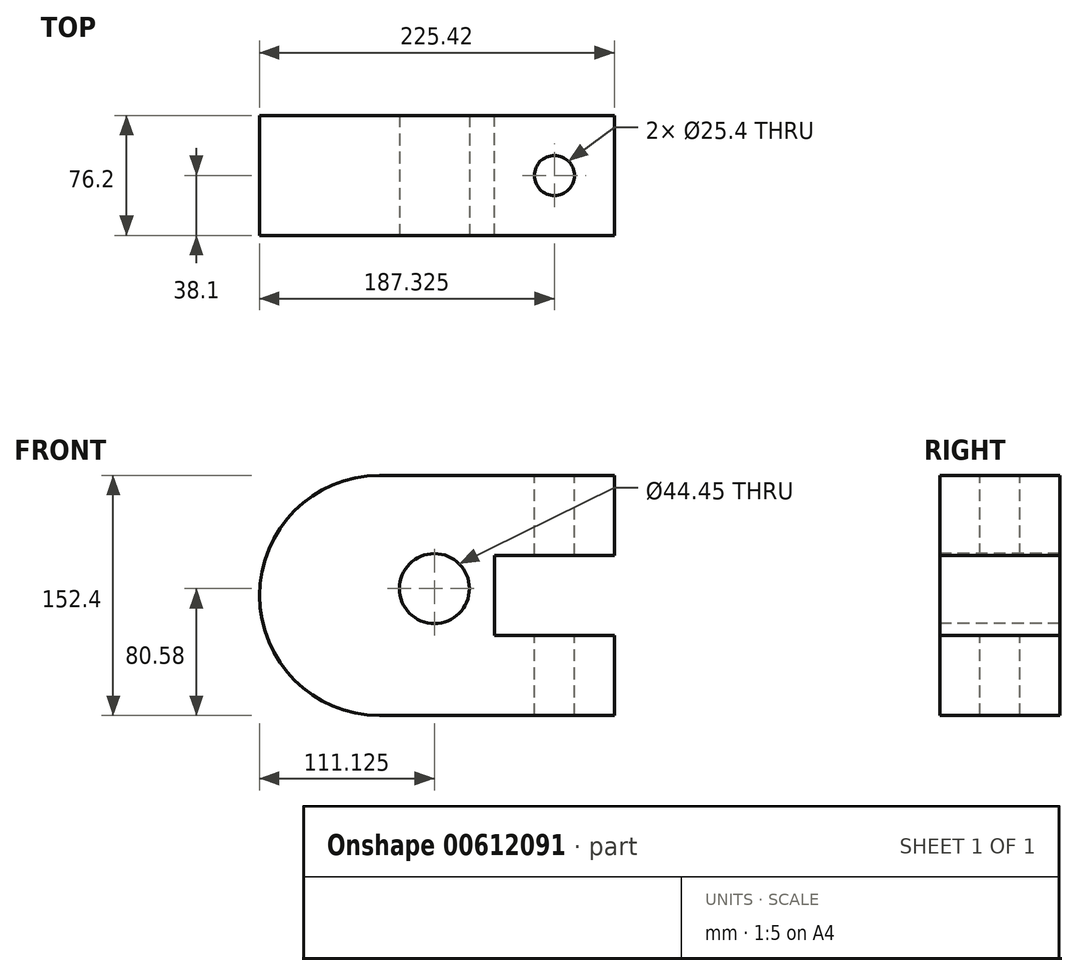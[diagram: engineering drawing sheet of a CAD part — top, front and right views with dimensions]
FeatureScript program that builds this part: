
annotation { "Feature Type Name" : "Feature", "Feature Type Description" : "" }
export const myFeature = defineFeature(function(context is Context, id is Id, definition is map)
    precondition{}
    {
        {
            var Q0;
            Q0=qCreatedBy(makeId("Front.planeOp"),FACE);
            var sketch = newSketch(context, id + "F0", { "sketchPlane" : qUnion([Q0])});
            skLineSegment(sketch, "E0", {"start": v(0, 0) * mm, "end": v(149.23, 0) * mm});
            skLineSegment(sketch, "E1", {"start": v(149.23, 0) * mm, "end": v(149.23, 50.8) * mm});
            skLineSegment(sketch, "E2", {"start": v(149.23, 50.8) * mm, "end": v(73.03, 50.8) * mm});
            skLineSegment(sketch, "E3", {"start": v(73.03, 50.8) * mm, "end": v(73.03, 101.6) * mm});
            skLineSegment(sketch, "E4", {"start": v(73.03, 101.6) * mm, "end": v(149.23, 101.6) * mm});
            skLineSegment(sketch, "E5", {"start": v(149.23, 101.6) * mm, "end": v(149.23, 152.4) * mm});
            skLineSegment(sketch, "E6", {"start": v(149.23, 152.4) * mm, "end": v(0, 152.4) * mm});
            skArc(sketch, "E7", {"start": v(0, 152.4) * mm, "mid": v(-76.2, 76.2) * mm, "end": v(0, 0) * mm});
            skSolve(sketch);
        }
        {
            var Q0;
            Q0=makeQuery(id+"F0.imprint","IMPRINT",FACE,{"disambiguationData":[TD([[makeQuery(id+"F0.imprint","IMPRINT",EDGE,{"derivedFrom":sQuery(id+"F0.wireOp",EDGE,"E0")}),1.0]])]});
            extrude(context, id + "F1", {"entities" : qUnion([Q0]), "depth" : 76.2 * mm, "offsetDistance" : 25.4 * mm});
        }
        {
            var Q0;
            Q0=makeQuery(id+"F1.opExtrude","CAP_FACE",FACE,{"disambiguationData":[OSD([sQuery(id+"F0.wireOp",EDGE,"E0"),sQuery(id+"F0.wireOp",EDGE,"E1"),sQuery(id+"F0.wireOp",EDGE,"E2"),sQuery(id+"F0.wireOp",EDGE,"E3"),sQuery(id+"F0.wireOp",EDGE,"E4"),sQuery(id+"F0.wireOp",EDGE,"E5"),sQuery(id+"F0.wireOp",EDGE,"E6"),sQuery(id+"F0.wireOp",EDGE,"E7")])],"isStart":false});
            var sketch = newSketch(context, id + "F2", { "sketchPlane" : qUnion([Q0])});
            skCircle(sketch, "E8", {"center": v(34.93, 80.58) * mm, "radius": 22.23 * mm});
            skSolve(sketch);
        }
        {
            var Q0;
            Q0=makeQuery(id+"F2.imprint","IMPRINT",FACE,{"disambiguationData":[TD([[makeQuery(id+"F2.imprint","IMPRINT",EDGE,{"derivedFrom":sQuery(id+"F2.wireOp",EDGE,"E8")}),1.0]])]});
            extrude(context, id + "F3", {"entities" : qUnion([Q0]), "operationType" : NewBodyOperationType.REMOVE, "oppositeDirection" : true, "depth" : 254 * mm, "offsetDistance" : 25.4 * mm});
        }
        {
            var Q0;
            Q0=makeQuery(id+"F1.opExtrude","SWEPT_FACE",FACE,{"disambiguationData":[OSD([sQuery(id+"F0.wireOp",EDGE,"E6")])]});
            var sketch = newSketch(context, id + "F4", { "sketchPlane" : qUnion([Q0])});
            skCircle(sketch, "E9", {"center": v(111.13, -38.1) * mm, "radius": 12.7 * mm});
            skSolve(sketch);
        }
        {
            var Q0;
            Q0=makeQuery(id+"F4.imprint","IMPRINT",FACE,{"disambiguationData":[TD([[makeQuery(id+"F4.imprint","IMPRINT",EDGE,{"derivedFrom":sQuery(id+"F4.wireOp",EDGE,"E9")}),1.0]])]});
            extrude(context, id + "F5", {"entities" : qUnion([Q0]), "operationType" : NewBodyOperationType.REMOVE, "oppositeDirection" : true, "depth" : 508 * mm, "offsetDistance" : 25.4 * mm});
        }
    });
